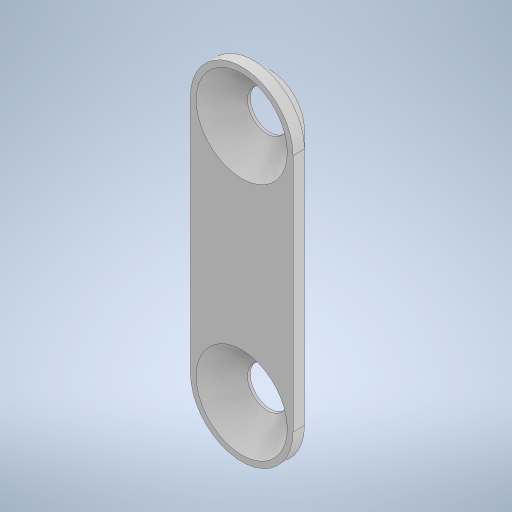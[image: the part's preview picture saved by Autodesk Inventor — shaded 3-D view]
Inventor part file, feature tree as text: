
AUTODESK INVENTOR PART (.ipt)
format: ipt  version: 2023 (Build 270158000, 158)  size: 276,480 bytes
history: native  units: in
note: dims shown in document units (in); Inventor stores cm internally (conversion verified against a paired STEP export)
features: other x5, sketch x3, reference x3, extrude x2, hole x1, chamfer x1, projected_geometry x1
ambient origin geometry x8: Origin, YZ Plane, XZ Plane, XY Plane, X Axis, Y Axis, Z Axis, Center Point
bodies: Body1 (feature_tree)
feature tree (16):
  other  "Bryła1"
  sketch  "Szkic1"
  other  "Płaszczyzna konstrukcyjna1"
  extrude  "Wyciągnięcie proste1"  Depth=0.3937in TaperAngle=0.0deg
  hole  "Otwór1"  [1 undecoded]
  extrude  "Wyciągnięcie proste2"  TaperAngle=0.0deg  [1 undecoded]
  chamfer  "Faza1"  Distance=0.0591in Angle=45.0deg
  reference  "Odniesienie1"
  sketch  "Szkic2"
  reference  "Odniesienie2"
  reference  "Odniesienie3"
  sketch  "Szkic3"
  projected_geometry  "Pętla rzutowana1"
  other  "<userpath>\Desktop\MojeRoboty\Stefan\mechanics 2\STEFAN.iam"
  other  "STEFAN.iam"
  other  "sciana_prawa_nowa:1"
note: 2 required parameter values undecoded (feature->parameter linkage not recoverable at this tier; creation-order binding heuristic only, values carry confidence <= 0.55)
